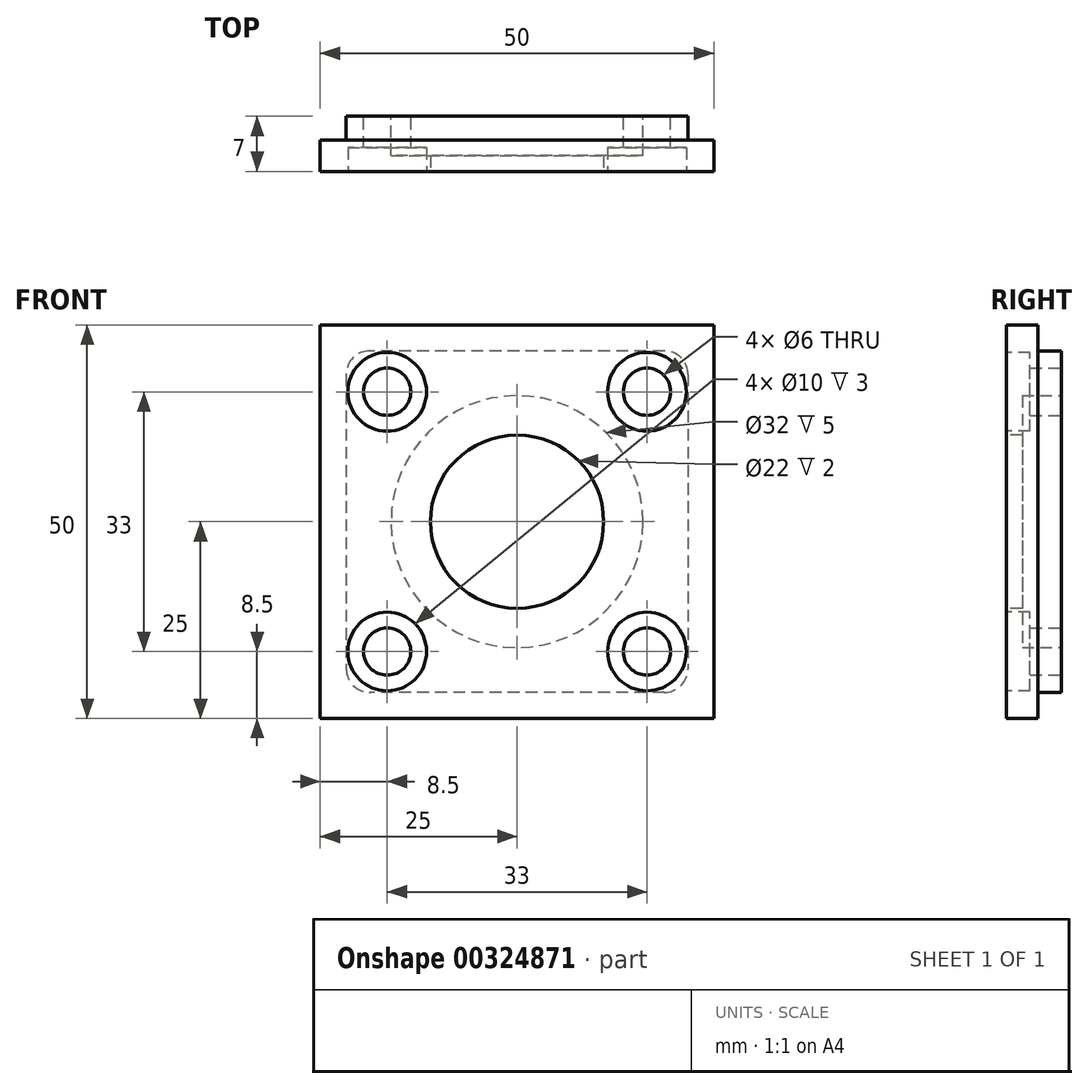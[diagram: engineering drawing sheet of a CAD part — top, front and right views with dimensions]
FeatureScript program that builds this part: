
annotation { "Feature Type Name" : "Feature", "Feature Type Description" : "" }
export const myFeature = defineFeature(function(context is Context, id is Id, definition is map)
    precondition{}
    {
        {
            var Q0;
            Q0=qCreatedBy(makeId("Front.planeOp"),FACE);
            var sketch = newSketch(context, id + "F0", { "sketchPlane" : qUnion([Q0])});
            skLineSegment(sketch, "E0.bottom", {"start": v(-25, 25) * mm, "end": v(25, 25) * mm});
            skLineSegment(sketch, "E0.top", {"start": v(-25, -25) * mm, "end": v(25, -25) * mm});
            skLineSegment(sketch, "E0.left", {"start": v(-25, 25) * mm, "end": v(-25, -25) * mm});
            skLineSegment(sketch, "E0.right", {"start": v(25, 25) * mm, "end": v(25, -25) * mm});
            skPoint(sketch, "E0.middle", {"position": v(0, 0) * mm});
            skSolve(sketch);
        }
        {
            var Q0;
            Q0=makeQuery(id+"F0.imprint","IMPRINT",FACE,{"disambiguationData":[TD([[makeQuery(id+"F0.imprint","IMPRINT",EDGE,{"derivedFrom":sQuery(id+"F0.wireOp",EDGE,"E0.bottom")}),-1.0]])]});
            extrude(context, id + "F1", {"entities" : qUnion([Q0]), "oppositeDirection" : true, "depth" : 4 * mm});
        }
        {
            var Q0;
            Q0=makeQuery(id+"F1.opExtrude","CAP_FACE",FACE,{"disambiguationData":[OSD([sQuery(id+"F0.wireOp",EDGE,"E0.bottom"),sQuery(id+"F0.wireOp",EDGE,"E0.top"),sQuery(id+"F0.wireOp",EDGE,"E0.left"),sQuery(id+"F0.wireOp",EDGE,"E0.right")])],"isStart":false});
            var sketch = newSketch(context, id + "F2", { "sketchPlane" : qUnion([Q0])});
            skLineSegment(sketch, "E1.bottom", {"start": v(-21.7, 21.7) * mm, "end": v(21.7, 21.7) * mm});
            skLineSegment(sketch, "E1.top", {"start": v(-21.7, -21.7) * mm, "end": v(21.7, -21.7) * mm});
            skLineSegment(sketch, "E1.left", {"start": v(-21.7, 21.7) * mm, "end": v(-21.7, -21.7) * mm});
            skLineSegment(sketch, "E1.right", {"start": v(21.7, 21.7) * mm, "end": v(21.7, -21.7) * mm});
            skPoint(sketch, "E1.middle", {"position": v(0, 0) * mm});
            skSolve(sketch);
        }
        {
            var Q0;
            Q0=makeQuery(id+"F2.imprint","IMPRINT",FACE,{"disambiguationData":[TD([[makeQuery(id+"F2.imprint","IMPRINT",EDGE,{"derivedFrom":sQuery(id+"F2.wireOp",EDGE,"E1.bottom")}),-1.0]])]});
            extrude(context, id + "F3", {"entities" : qUnion([Q0]), "operationType" : NewBodyOperationType.ADD, "depth" : 3 * mm});
        }
        {
            var Q0;
            Q0=makeQuery(id+"F3.opExtrude","CAP_FACE",FACE,{"disambiguationData":[OSD([sQuery(id+"F2.wireOp",EDGE,"E1.bottom"),sQuery(id+"F2.wireOp",EDGE,"E1.top"),sQuery(id+"F2.wireOp",EDGE,"E1.left"),sQuery(id+"F2.wireOp",EDGE,"E1.right")])],"isStart":false});
            var sketch = newSketch(context, id + "F4", { "sketchPlane" : qUnion([Q0])});
            skLineSegment(sketch, "E2", {"start": v(-21.7, 21.7) * mm, "end": v(21.7, -21.7) * mm, "construction": true});
            skLineSegment(sketch, "E3", {"start": v(21.7, 21.7) * mm, "end": v(-21.7, -21.7) * mm, "construction": true});
            skLineSegment(sketch, "E4.bottom", {"start": v(-16.5, 16.5) * mm, "end": v(16.5, 16.5) * mm, "construction": true});
            skLineSegment(sketch, "E4.top", {"start": v(-16.5, -16.5) * mm, "end": v(16.5, -16.5) * mm, "construction": true});
            skLineSegment(sketch, "E4.left", {"start": v(-16.5, 16.5) * mm, "end": v(-16.5, -16.5) * mm, "construction": true});
            skLineSegment(sketch, "E4.right", {"start": v(16.5, 16.5) * mm, "end": v(16.5, -16.5) * mm, "construction": true});
            skPoint(sketch, "E4.middle", {"position": v(0, 0) * mm});
            skCircle(sketch, "E5", {"center": v(-16.5, 16.5) * mm, "radius": 3 * mm});
            skCircle(sketch, "E6", {"center": v(16.5, 16.5) * mm, "radius": 3 * mm});
            skCircle(sketch, "E7", {"center": v(-16.5, -16.5) * mm, "radius": 3 * mm});
            skCircle(sketch, "E8", {"center": v(16.5, -16.5) * mm, "radius": 3 * mm});
            skSolve(sketch);
        }
        {
            var Q0;
            Q0=makeQuery(id+"F4.imprint","IMPRINT",FACE,{"disambiguationData":[TD([[makeQuery(id+"F4.imprint","IMPRINT",EDGE,{"derivedFrom":sQuery(id+"F4.wireOp",EDGE,"E5")}),1.0]])]});
            var Q1;
            Q1=makeQuery(id+"F4.imprint","IMPRINT",FACE,{"disambiguationData":[TD([[makeQuery(id+"F4.imprint","IMPRINT",EDGE,{"derivedFrom":sQuery(id+"F4.wireOp",EDGE,"E6")}),1.0]])]});
            var Q2;
            Q2=makeQuery(id+"F4.imprint","IMPRINT",FACE,{"disambiguationData":[TD([[makeQuery(id+"F4.imprint","IMPRINT",EDGE,{"derivedFrom":sQuery(id+"F4.wireOp",EDGE,"E8")}),1.0]])]});
            var Q3;
            Q3=makeQuery(id+"F4.imprint","IMPRINT",FACE,{"disambiguationData":[TD([[makeQuery(id+"F4.imprint","IMPRINT",EDGE,{"derivedFrom":sQuery(id+"F4.wireOp",EDGE,"E7")}),1.0]])]});
            var Q4;
            Q4=makeQuery(id+"F4.imprint","IMPRINT",FACE,{"disambiguationData":[TD([[makeQuery(id+"F4.imprint","IMPRINT",EDGE,{"derivedFrom":sQuery(id+"F4.wireOp",EDGE,"QwKJkzou-eQ0R-DmLM-VaWs-TZL8aThNHikG")}),1.0]])]});
            extrude(context, id + "F5", {"entities" : qUnion([Q0, Q1, Q2, Q3, Q4]), "operationType" : NewBodyOperationType.REMOVE, "oppositeDirection" : true, "depth" : 25 * mm});
        }
        {
            var Q0;
            Q0=makeQuery(id+"F1.opExtrude","CAP_FACE",FACE,{"disambiguationData":[OSD([sQuery(id+"F0.wireOp",EDGE,"E0.bottom"),sQuery(id+"F0.wireOp",EDGE,"E0.top"),sQuery(id+"F0.wireOp",EDGE,"E0.left"),sQuery(id+"F0.wireOp",EDGE,"E0.right")])],"isStart":true});
            var sketch = newSketch(context, id + "F6", { "sketchPlane" : qUnion([Q0])});
            skCircle(sketch, "E9", {"center": v(-16.5, 16.5) * mm, "radius": 5 * mm});
            skCircle(sketch, "E10.1.0", {"center": v(-16.5, -16.5) * mm, "radius": 5 * mm});
            skCircle(sketch, "E10.2.0", {"center": v(16.5, -16.5) * mm, "radius": 5 * mm});
            skCircle(sketch, "E10.3.0", {"center": v(16.5, 16.5) * mm, "radius": 5 * mm});
            skPoint(sketch, "E10.center", {"position": v(0, 0) * mm});
            skSolve(sketch);
        }
        {
            var Q0;
            Q0=makeQuery(id+"F6.imprint","IMPRINT",FACE,{"disambiguationData":[TD([[makeQuery(id+"F6.imprint","IMPRINT",EDGE,{"derivedFrom":sQuery(id+"F6.wireOp",EDGE,"E9")}),1.0]])]});
            var Q1;
            Q1=makeQuery(id+"F6.imprint","IMPRINT",FACE,{"disambiguationData":[TD([[makeQuery(id+"F6.imprint","IMPRINT",EDGE,{"derivedFrom":sQuery(id+"F6.wireOp",EDGE,"E10.3.0")}),1.0]])]});
            var Q2;
            Q2=makeQuery(id+"F6.imprint","IMPRINT",FACE,{"disambiguationData":[TD([[makeQuery(id+"F6.imprint","IMPRINT",EDGE,{"derivedFrom":sQuery(id+"F6.wireOp",EDGE,"E10.2.0")}),1.0]])]});
            var Q3;
            Q3=makeQuery(id+"F6.imprint","IMPRINT",FACE,{"disambiguationData":[TD([[makeQuery(id+"F6.imprint","IMPRINT",EDGE,{"derivedFrom":sQuery(id+"F6.wireOp",EDGE,"E10.1.0")}),1.0]])]});
            extrude(context, id + "F7", {"entities" : qUnion([Q0, Q1, Q2, Q3]), "operationType" : NewBodyOperationType.REMOVE, "oppositeDirection" : true, "depth" : 3 * mm});
        }
        {
            var Q0;
            Q0=makeQuery(id+"F3.opExtrude","CAP_FACE",FACE,{"disambiguationData":[OSD([sQuery(id+"F2.wireOp",EDGE,"E1.bottom"),sQuery(id+"F2.wireOp",EDGE,"E1.top"),sQuery(id+"F2.wireOp",EDGE,"E1.left"),sQuery(id+"F2.wireOp",EDGE,"E1.right")])],"isStart":false});
            var sketch = newSketch(context, id + "F8", { "sketchPlane" : qUnion([Q0])});
            skCircle(sketch, "E11", {"center": v(0, 0) * mm, "radius": 16 * mm});
            skSolve(sketch);
        }
        {
            var Q0;
            Q0=makeQuery(id+"F8.imprint","IMPRINT",FACE,{"disambiguationData":[TD([[makeQuery(id+"F8.imprint","IMPRINT",EDGE,{"derivedFrom":sQuery(id+"F8.wireOp",EDGE,"E11")}),1.0]])]});
            extrude(context, id + "F9", {"entities" : qUnion([Q0]), "operationType" : NewBodyOperationType.REMOVE, "oppositeDirection" : true, "depth" : 5 * mm});
        }
        {
            var Q0;
            Q0=makeQuery(id+"F1.opExtrude","CAP_FACE",FACE,{"disambiguationData":[OSD([sQuery(id+"F0.wireOp",EDGE,"E0.bottom"),sQuery(id+"F0.wireOp",EDGE,"E0.top"),sQuery(id+"F0.wireOp",EDGE,"E0.left"),sQuery(id+"F0.wireOp",EDGE,"E0.right")])],"isStart":true});
            var sketch = newSketch(context, id + "F10", { "sketchPlane" : qUnion([Q0])});
            skCircle(sketch, "E12", {"center": v(0, 0) * mm, "radius": 11 * mm});
            skSolve(sketch);
        }
        {
            var Q0;
            Q0=makeQuery(id+"F10.imprint","IMPRINT",FACE,{"disambiguationData":[TD([[makeQuery(id+"F10.imprint","IMPRINT",EDGE,{"derivedFrom":sQuery(id+"F10.wireOp",EDGE,"E12")}),1.0]])]});
            extrude(context, id + "F11", {"entities" : qUnion([Q0]), "operationType" : NewBodyOperationType.REMOVE, "oppositeDirection" : true, "depth" : 25 * mm});
        }
        {
            var Q0;
            Q0=makeQuery(id+"F3.opExtrude","SWEPT_EDGE",EDGE,{"disambiguationData":[OSD([sQuery(id+"F2.wireOp",EDGE,"E1.bottom"),sQuery(id+"F2.wireOp",EDGE,"E1.left")])]});
            var Q1;
            Q1=makeQuery(id+"F3.opExtrude","SWEPT_EDGE",EDGE,{"disambiguationData":[OSD([sQuery(id+"F2.wireOp",EDGE,"E1.bottom"),sQuery(id+"F2.wireOp",EDGE,"E1.right")])]});
            var Q2;
            Q2=makeQuery(id+"F3.opExtrude","SWEPT_EDGE",EDGE,{"disambiguationData":[OSD([sQuery(id+"F2.wireOp",EDGE,"E1.top"),sQuery(id+"F2.wireOp",EDGE,"E1.right")])]});
            var Q3;
            Q3=makeQuery(id+"F3.opExtrude","SWEPT_EDGE",EDGE,{"disambiguationData":[OSD([sQuery(id+"F2.wireOp",EDGE,"E1.top"),sQuery(id+"F2.wireOp",EDGE,"E1.left")])]});
            fillet(context, id + "F12", {"entities" : qUnion([Q0, Q1, Q2, Q3]), "radius" : 3 * mm, "tangentPropagation" : true, "allowEdgeOverflow" : false});
        }
    });
